# Revit family: 111110004403001
name_source: partatom
category: Generic Models
revit_build: Autodesk Revit 2018 (Build: 20190510_1515(x64)
units: mm (PartAtom-declared; Revit-internal decimal feet)

## family parameters
Can host rebar = No
Cut with Voids When Loaded = No
Host = Face
Part Type = Normal
Room Calculation Point = No
Round Connector Dimension = Use Diameter
Shared = No

## types (1)
- CELOSIA CON PESTANA PP 17X17CM BLANCO
    Aplicacion = Se utiliza como sistema de ventilación en puertas, muro y tinas
    Color = Blanco
    Default Elevation = 1000 mm  [stored 3.28084 ft]
    Description = Celosía plana 17x17
    Dimension = 170 mm  [stored 0.557743 ft]
    Empresa = CNP SPA.
    Espesor = 1 mm  [stored 0.00328084 ft]
    Largo = 170 mm  [stored 0.557743 ft]
    Material = PP Blanco
    Model = CELOSIA CON PESTANA
    Nombre SKU = CELOSIA CON PESTANA PP 17X17CM BLANCO
    Num SKUs = 111110004403001
    URL = https://www.empresascnp.cl
    Unidad = Por unidad
    Url Ficha tecnica = https://empresascnp.cl
    Uso = Se utiliza como sistema de ventilación en Puertas, Shaft, Muro y Tina

note: [stored X ft] marks values corroborated as IEEE doubles in the binary element streams (Revit-internal decimal feet)

## geometry (parser evidence)
native form markers: Sweep x10
no freeform markers — native parametric forms only
